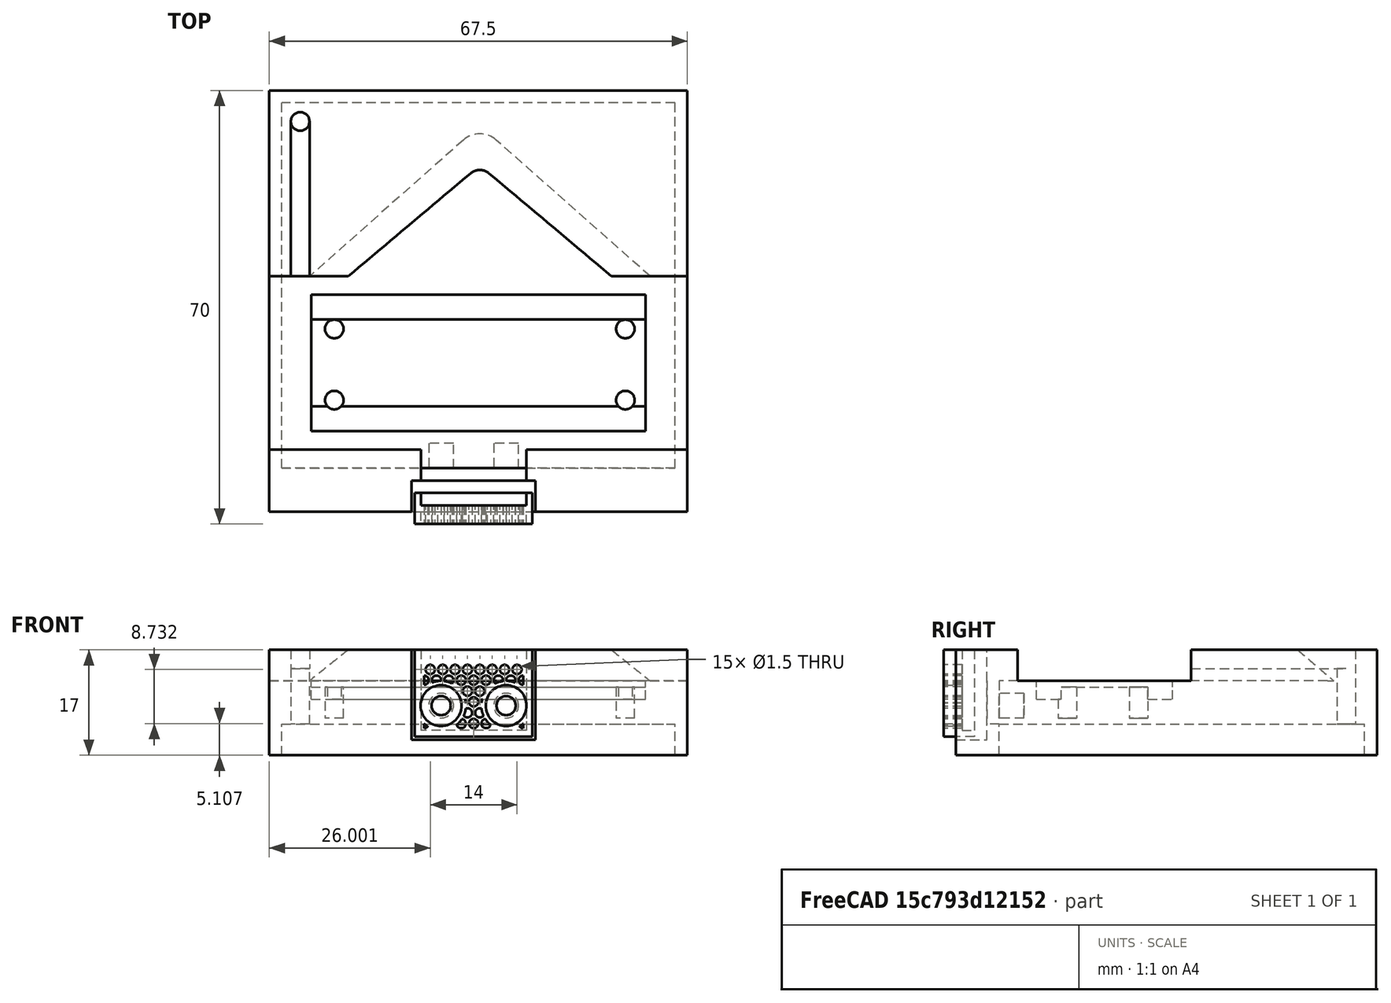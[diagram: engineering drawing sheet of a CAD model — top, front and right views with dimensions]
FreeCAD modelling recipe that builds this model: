
FCSTD DOCUMENT  (FreeCAD 0.20R29410 (Git))
Label: Weatherstation
License: All rights reserved
LicenseURL: https://en.wikipedia.org/wiki/All_rights_reserved
objects: Part::Cylinder×13, Part::Box×10, Sketcher::SketchObject×8, PartDesign::Body×6, PartDesign::Pad×5, Part::Cut×5, Part::MultiFuse×4, Part::FeaturePython×3, Mesh::Feature×2, Part::Extrusion×1, PartDesign::AdditiveLoft×1, Part::MultiCommon×1
note: 62 computed .brp shape members not serialized (recipe doc carries the construction recipe); baked Part::Feature solids carry a one-line shape summary decoded from their .brp

FEATURE [Sketcher::SketchObject] Sketch
  FullyConstrained = true
  MapMode = 5
  Support = -> [XY_Plane]
  sketch-geometry (4):
    g0: LineSegment StartX=19 StartY=19 StartZ=0 EndX=86.5 EndY=19 EndZ=0
    g1: LineSegment StartX=86.5 StartY=19 StartZ=0 EndX=86.5 EndY=82 EndZ=0
    g2: LineSegment StartX=86.5 StartY=82 StartZ=0 EndX=19 EndY=82 EndZ=0
    g3: LineSegment StartX=19 StartY=82 StartZ=0 EndX=19 EndY=19 EndZ=0
  constraints (12):
    c: Coincident(g0,g1)
    c: Coincident(g1,g2)
    c: Coincident(g2,g3)
    c: Coincident(g3,g0)
    c: Horizontal(g0)
    c: Horizontal(g2)
    c: Vertical(g1)
    c: Vertical(g3)
    c: DistanceX(g-1,g0) = 19
    c: DistanceY(g-1,g0) = 19
    c: DistanceY(g1,g1) = 63
    c: DistanceX(g0,g0) = 67.5
FEATURE [PartDesign::Pad] Pad
  Direction = (0,0,1)
  Length = 12
  Length2 = 10
  Profile = -> Sketch
  ReferenceAxis = -> Sketch [N_Axis]
  Type = 0
FEATURE [PartDesign::Body] Body  label="Base"
  Group = -> [Sketch,Pad]
  Origin = -> Origin
  Placement = pos=(0,0,-2) rot=(0,0,1;0rad)
  Tip = -> Pad
FEATURE [Sketcher::SketchObject] Sketch001
  FullyConstrained = true
  MapMode = 5
  Support = -> [XY_Plane001]
  sketch-geometry (4):
    g0: LineSegment StartX=22.75 StartY=49 StartZ=0 EndX=76.75 EndY=49 EndZ=0
    g1: LineSegment StartX=76.75 StartY=49 StartZ=0 EndX=76.75 EndY=27 EndZ=0
    g2: LineSegment StartX=76.75 StartY=27 StartZ=0 EndX=22.75 EndY=27 EndZ=0
    g3: LineSegment StartX=22.75 StartY=27 StartZ=0 EndX=22.75 EndY=49 EndZ=0
  constraints (12):
    c: Coincident(g0,g1)
    c: Coincident(g1,g2)
    c: Coincident(g2,g3)
    c: Coincident(g3,g0)
    c: Horizontal(g0)
    c: Horizontal(g2)
    c: Vertical(g1)
    c: Vertical(g3)
    c: DistanceX(g0,g0) = 54
    c: DistanceY(g1,g1) = 22
    c: DistanceX(g-1,g2) = 22.75
    c: DistanceY(g-1,g2) = 27
FEATURE [PartDesign::Pad] Pad001
  Direction = (0,0,1)
  Length = 2
  Length2 = 10
  Profile = -> Sketch001
  ReferenceAxis = -> Sketch001 [N_Axis]
  Type = 0
FEATURE [PartDesign::Body] Body001  label="Pico sink"
  Group = -> [Sketch001,Pad001]
  Origin = -> Origin001
  Placement = pos=(0,0,9) rot=(0,0,1;0rad)
  Tip = -> Pad001
FEATURE [Part::Cylinder] Cylinder  label="Pico Screw 1"
  Angle = 360
  AttacherType = Attacher::AttachEngine3D
  FirstAngle = 0
  Height = 10
  Placement = pos=(26.5,32,4) rot=(0,0,1;0rad)
  Radius = 1.5
  SecondAngle = 0
FEATURE [Part::Cylinder] Cylinder001  label="Pico Screw 2"
  Angle = 360
  AttacherType = Attacher::AttachEngine3D
  FirstAngle = 0
  Height = 10
  Placement = pos=(26.5,43.5,4) rot=(0,0,1;0rad)
  Radius = 1.5
  SecondAngle = 0
FEATURE [Part::Cylinder] Cylinder002  label="Pico Screw 3"
  Angle = 360
  AttacherType = Attacher::AttachEngine3D
  FirstAngle = 0
  Height = 10
  Placement = pos=(73.5,43.5,4) rot=(0,0,1;0rad)
  Radius = 1.5
  SecondAngle = 0
FEATURE [Part::Cylinder] Cylinder003  label="Pico Screw 4"
  Angle = 360
  AttacherType = Attacher::AttachEngine3D
  FirstAngle = 0
  Height = 10
  Placement = pos=(73.5,32,4) rot=(0,0,1;0rad)
  Radius = 1.5
  SecondAngle = 0
FEATURE [Part::Cylinder] Cylinder004  label="bme280 screw 1"
  Angle = 360
  AttacherType = Attacher::AttachEngine3D
  FirstAngle = 0
  Height = 10
  Placement = pos=(45.75,26,8) rot=(1,0,0;1.5708rad)
  Radius = 2
  SecondAngle = 0
FEATURE [Part::Cylinder] Cylinder005  label="bme280 screw 2"
  Angle = 360
  AttacherType = Attacher::AttachEngine3D
  FirstAngle = 0
  Height = 10
  Placement = pos=(56.25,26,8) rot=(1,0,0;1.5708rad)
  Radius = 2
  SecondAngle = 0
FEATURE [Sketcher::SketchObject] Sketch002
  FullyConstrained = true
  MapMode = 5
  Placement = pos=(0,0,0) rot=(1,0,0;1.5708rad)
  Support = -> [XZ_Plane002]
  sketch-geometry (4):
    g0: LineSegment StartX=41.5 StartY=13 StartZ=0 EndX=60.5 EndY=13 EndZ=0
    g1: LineSegment StartX=60.5 StartY=13 StartZ=0 EndX=60.5 EndY=-1 EndZ=0
    g2: LineSegment StartX=60.5 StartY=-1 StartZ=0 EndX=41.5 EndY=-1 EndZ=0
    g3: LineSegment StartX=41.5 StartY=-1 StartZ=0 EndX=41.5 EndY=13 EndZ=0
  constraints (12):
    c: Coincident(g0,g1)
    c: Coincident(g1,g2)
    c: Coincident(g2,g3)
    c: Coincident(g3,g0)
    c: Horizontal(g0)
    c: Horizontal(g2)
    c: Vertical(g1)
    c: Vertical(g3)
    c: DistanceX(g0,g0) = 19
    c: DistanceY(g1,g1) = 14
    c: DistanceX(g-1,g2) = 41.5
    c: DistanceY(g-1,g2) = -1
FEATURE [PartDesign::Pad] Pad002
  Direction = (0,-1,-2e-16)
  Length = 5
  Length2 = 10
  Placement = pos=(0,0,0) rot=(1,0,0;1.5708rad)
  Profile = -> Sketch002
  ReferenceAxis = -> Sketch002 [N_Axis]
  Type = 0
FEATURE [PartDesign::Body] Body002  label="bme280 protector"
  Group = -> [Sketch002,Pad002]
  Origin = -> Origin002
  Placement = pos=(0,17,0) rot=(0,0,1;0rad)
  Tip = -> Pad002
FEATURE [Part::Box] Box  label="bme280 hole"
  AttacherType = Attacher::AttachEngine3D
  Height = 12
  Length = 17
  Placement = pos=(42.5,20,-1) rot=(0,0,1;0rad)
  Width = 2
FEATURE [Part::Cylinder] Cylinder006  label="bme280 screw 3"
  Angle = 360
  AttacherType = Attacher::AttachEngine3D
  FirstAngle = 0
  Height = 10
  Placement = pos=(45.75,20,7) rot=(1,0,0;1.5708rad)
  Radius = 1.55
  SecondAngle = 0
FEATURE [Part::Cylinder] Cylinder007  label="bme280 screw 4"
  Angle = 360
  AttacherType = Attacher::AttachEngine3D
  FirstAngle = 0
  Height = 10
  Placement = pos=(56.25,20,7) rot=(1,0,0;1.5708rad)
  Radius = 1.55
  SecondAngle = 0
FEATURE [Part::Box] Box001  label="Pico Con 1"
  AttacherType = Attacher::AttachEngine3D
  Height = 2
  Length = 54
  Placement = pos=(22.75,45,7) rot=(0,0,1;0rad)
  Width = 4
FEATURE [Part::Box] Box002  label="Pico Con 2"
  AttacherType = Attacher::AttachEngine3D
  Height = 2
  Length = 54
  Placement = pos=(22.75,27,7) rot=(0,0,1;0rad)
  Width = 4
FEATURE [Part::Box] Box003  label="bme280 Iron 1"
  AttacherType = Attacher::AttachEngine3D
  Height = 5
  Length = 17
  Placement = pos=(42.5,17,-1) rot=(0,0,1;0rad)
  Width = 5
FEATURE [Part::FeaturePython] BooleanFragments001  label="bme280"  # WARN: FeaturePython — macro-defined, semantics opaque (R4)
  Mode = 0
  Objects = -> [Cylinder005,Cylinder004,Box003,Box]
  Placement = pos=(1,41,14) rot=(1,0,0;3.14159rad)
  Tolerance = 0
FEATURE [Part::Box] Box004  label="Power Pack"
  AttacherType = Attacher::AttachEngine3D
  Height = 15
  Length = 63.5
  Placement = pos=(21,21,-12) rot=(0,0,1;0rad)
  Width = 59
FEATURE [Part::Cylinder] Cylinder008  label="bme280 screw 005"
  Angle = 360
  AttacherType = Attacher::AttachEngine3D
  FirstAngle = 0
  Height = 2
  Placement = pos=(45.75,14,7) rot=(1,0,0;1.5708rad)
  Radius = 3.3
  SecondAngle = 0
FEATURE [Part::Cylinder] Cylinder009  label="bme280 screw 006"
  Angle = 360
  AttacherType = Attacher::AttachEngine3D
  FirstAngle = 0
  Height = 2
  Placement = pos=(56.25,14,7) rot=(1,0,0;1.5708rad)
  Radius = 3.3
  SecondAngle = 0
FEATURE [Part::Box] Box005  label="bme281"
  AttacherType = Attacher::AttachEngine3D
  Height = 14
  Length = 17
  Placement = pos=(42.5,15,-3) rot=(0,0,1;0rad)
  Width = 2
FEATURE [Sketcher::SketchObject] Sketch003
  FullyConstrained = false
  Placement = pos=(0,0,0) rot=(1,0,0;1.5708rad)
  sketch-geometry (5):
    g0: Circle CenterX=7.86917 CenterY=53.8929 CenterZ=0 NormalX=0 NormalY=0 NormalZ=1 AngleXU=0 Radius=0.75
    g1: LineSegment StartX=7.86917 StartY=53.8929 StartZ=0 EndX=9.86917 EndY=53.8929 EndZ=0
    g2: LineSegment StartX=9.86917 StartY=53.8929 StartZ=0 EndX=8.86917 EndY=52.1609 EndZ=0
    g3: LineSegment StartX=8.86917 StartY=52.1609 StartZ=0 EndX=7.86917 EndY=53.8929 EndZ=0
    g4: Circle CenterX=8.86917 CenterY=52.1609 CenterZ=0 NormalX=0 NormalY=0 NormalZ=1 AngleXU=0 Radius=0.75
  constraints (11):
    c: Radius(g0) = 0.75
    c: Coincident(g1,g0)
    c: Horizontal(g1)
    c: Coincident(g1,g2)
    c: Coincident(g2,g3)
    c: Coincident(g3,g1)
    c: DistanceX(g1,g1) = 2
    c: Equal(g1,g2)
    c: Equal(g2,g3)
    c: Coincident(g4,g2)
    c: Equal(g0,g4)
FEATURE [Part::FeaturePython] Array  # Draft array (typed FeaturePython)
  AlwaysSyncPlacement = false
  Angle = 360
  ArrayType = 0
  Axis = (0,0,1)
  Base = -> Sketch003
  Center = (0,0,0)
  Count = 30
  ExpandArray = false
  Fuse = false
  IntervalAxis = (0,0,0)
  IntervalX = (2,0,0)
  IntervalY = (0,2,0)
  IntervalZ = (0,0,3.5)
  NumberCircles = 3
  NumberPolar = 5
  NumberX = 10
  NumberY = 1
  NumberZ = 3
  Placement = pos=(33.13,0,-51) rot=(0,0,1;0rad)
  PlacementList = 30 placements: [(0,0,0),(0,0,3.5),(0,0,7),(2,0,0),(2,0,3.5),(2,0,7),(4,0,0),(4,0,3.5),(4,0,7),(6,0,0),(6,0,3.5),(6,0,7),(8,0,0),(8,0,3.5),(8,0,7),(10,0,0),(10,0,3.5),(10,0,7),(12,0,0),(12,0,3.5),(12,0,7),(14,0,0),(14,0,3.5),(14,0,7),(16,0,0),(16,0,3.5),(16,0,7),(18,0,0),(18,0,3.5),(18,0,7)]
  RadialDistance = 50
  ScaleList = (30) [(1,1,1),(1,1,1),(1,1,1),(1,1,1),(1,1,1),(1,1,1),(1,1,1),(1,1,1),(1,1,1),(1,1,1),(1,1,1),(1,1,1),(1,1,1),(1,1,1),(1,1,1),(1,1,1),(1,1,1),(1,1,1),+12 more]
  Symmetry = 1
  TangentialDistance = 25
FEATURE [Part::Extrusion] Extrude
  Base = -> Array
  Dir = (0,1,0)
  DirMode = 2
  FaceMakerClass = Part::FaceMakerBullseye
  LengthFwd = 10
  LengthRev = 0
  Placement = pos=(0,8,0) rot=(0,0,1;0rad)
  Solid = true
  Symmetric = false
FEATURE [Part::Box] Box006  label="bme282"
  AttacherType = Attacher::AttachEngine3D
  Height = 12
  Length = 16
  Placement = pos=(43,9,-1) rot=(0,0,1;0rad)
  Width = 12
FEATURE [Part::Cylinder] Cylinder010  label="bme280 screw 007"
  Angle = 360
  AttacherType = Attacher::AttachEngine3D
  FirstAngle = 0
  Height = 18
  Placement = pos=(45.75,26,7) rot=(1,0,0;1.5708rad)
  Radius = 4
  SecondAngle = 0
FEATURE [Part::Cylinder] Cylinder011  label="bme280 screw 008"
  Angle = 360
  AttacherType = Attacher::AttachEngine3D
  FirstAngle = 0
  Height = 20
  Placement = pos=(56.25,26,7) rot=(1,0,0;1.5708rad)
  Radius = 4
  SecondAngle = 0
FEATURE [Sketcher::SketchObject] Sketch004
  FullyConstrained = true
  MapMode = 5
  Support = -> [XY_Plane003]
  sketch-geometry (4):
    g0: LineSegment StartX=19 StartY=52 StartZ=0 EndX=86.5 EndY=52 EndZ=0
    g1: LineSegment StartX=86.5 StartY=52 StartZ=0 EndX=86.5 EndY=82 EndZ=0
    g2: LineSegment StartX=86.5 StartY=82 StartZ=0 EndX=19 EndY=82 EndZ=0
    g3: LineSegment StartX=19 StartY=82 StartZ=0 EndX=19 EndY=52 EndZ=0
  constraints (12):
    c: Coincident(g0,g1)
    c: Coincident(g1,g2)
    c: Coincident(g2,g3)
    c: Coincident(g3,g0)
    c: Horizontal(g0)
    c: Horizontal(g2)
    c: Vertical(g1)
    c: Vertical(g3)
    c: DistanceX(g-1,g0) = 19
    c: DistanceY(g1,g1) = 30
    c: DistanceX(g0,g0) = 67.5
    c: DistanceY(g-1,g2) = 82
FEATURE [PartDesign::Pad] Pad003
  Direction = (0,0,1)
  Length = 5
  Length2 = 10
  Profile = -> Sketch004
  ReferenceAxis = -> Sketch004 [N_Axis]
  Type = 0
FEATURE [PartDesign::Body] Body003  label="top base"
  Group = -> [Sketch004,Pad003]
  Origin = -> Origin003
  Placement = pos=(0,0,10) rot=(0,0,1;0rad)
  Tip = -> Pad003
FEATURE [Sketcher::SketchObject] Sketch005
  FullyConstrained = true
  MapMode = 5
  Support = -> [XY_Plane004]
  sketch-geometry (4):
    g0: LineSegment StartX=19 StartY=19 StartZ=0 EndX=86.5 EndY=19 EndZ=0
    g1: LineSegment StartX=86.5 StartY=19 StartZ=0 EndX=86.5 EndY=24 EndZ=0
    g2: LineSegment StartX=86.5 StartY=24 StartZ=0 EndX=19 EndY=24 EndZ=0
    g3: LineSegment StartX=19 StartY=24 StartZ=0 EndX=19 EndY=19 EndZ=0
  constraints (12):
    c: Coincident(g0,g1)
    c: Coincident(g1,g2)
    c: Coincident(g2,g3)
    c: Coincident(g3,g0)
    c: Horizontal(g0)
    c: Horizontal(g2)
    c: Vertical(g1)
    c: Vertical(g3)
    c: DistanceX(g-1,g0) = 19
    c: DistanceY(g1,g1) = 5
    c: DistanceX(g0,g0) = 67.5
    c: DistanceY(g-1,g0) = 19
FEATURE [PartDesign::Pad] Pad004
  Direction = (0,0,1)
  Length = 5
  Length2 = 10
  Profile = -> Sketch005
  ReferenceAxis = -> Sketch005 [N_Axis]
  Type = 0
FEATURE [PartDesign::Body] Body004  label="bottom base"
  Group = -> [Sketch005,Pad004]
  Origin = -> Origin004
  Placement = pos=(0,0,10) rot=(0,0,1;0rad)
  Tip = -> Pad004
FEATURE [Sketcher::SketchObject] Sketch008
  FullyConstrained = true
  MapMode = 5
  Placement = pos=(0,0,6) rot=(0,0,1;0rad)
  sketch-geometry (4):
    g0: LineSegment StartX=33 StartY=51 StartZ=0 EndX=51.7227 EndY=66.539 EndZ=0
    g1: LineSegment StartX=54.2773 StartY=66.539 StartZ=0 EndX=73 EndY=51 EndZ=0
    g2: LineSegment StartX=73 StartY=51 StartZ=0 EndX=33 EndY=51 EndZ=0
    g3: ArcOfCircle CenterX=53 CenterY=65 CenterZ=0 NormalX=0 NormalY=0 NormalZ=1 AngleXU=0 Radius=2 StartAngle=0.878055 EndAngle=2.26354
  constraints (11):
    c: Coincident(g1,g2)
    c: Coincident(g2,g0)
    c: Horizontal(g2)
    c: Equal(g0,g1)
    c: DistanceX(g0,g1) = 40
    c: DistanceY(g-1,g0) = 51
    c: Tangent(g0,g3) = 1.5708
    c: Tangent(g1,g3) = 1.5708
    c: Radius(g3) = 2
    c: DistanceX(g-1,g3) = 53
    c: DistanceY(g-1,g3) = 65
FEATURE [Sketcher::SketchObject] Sketch009
  FullyConstrained = true
  MapMode = 5
  sketch-geometry (4):
    g0: LineSegment StartX=50.3488 StartY=72.9952 StartZ=0 EndX=25.5 EndY=51 EndZ=0
    g1: LineSegment StartX=25.5 StartY=51 StartZ=0 EndX=80.5 EndY=51 EndZ=0
    g2: LineSegment StartX=80.5 StartY=51 StartZ=0 EndX=55.6512 EndY=72.9952 EndZ=0
    g3: ArcOfCircle CenterX=53 CenterY=70 CenterZ=0 NormalX=0 NormalY=0 NormalZ=1 AngleXU=0 Radius=4 StartAngle=0.84624 EndAngle=2.29535
  constraints (11):
    c: Coincident(g0,g1)
    c: Horizontal(g1)
    c: Coincident(g1,g2)
    c: Equal(g2,g0)
    c: Tangent(g0,g3) = -1.5708
    c: Tangent(g2,g3) = -1.5708
    c: Radius(g3) = 4
    c: DistanceX(g1,g1) = 55
    c: DistanceX(g-1,g3) = 53
    c: DistanceY(g-1,g0) = 51
    c: DistanceY(g-1,g3) = 70
FEATURE [PartDesign::AdditiveLoft] AdditiveLoft
  Closed = false
  Placement = pos=(0,0,6) rot=(0,0,1;0rad)
  Profile = -> Sketch008
  Ruled = false
  Sections = -> [Sketch009]
FEATURE [PartDesign::Body] Body006  label="Anker"
  Group = -> [Sketch009,Sketch008,AdditiveLoft]
  Origin = -> Origin006
  Placement = pos=(0,1,10) rot=(0,0,1;0rad)
  Tip = -> AdditiveLoft
FEATURE [Part::MultiCommon] Common  label="Grid"
  Shapes = -> [Box006,Extrude]
FEATURE [Part::MultiFuse] Fusion  label="Screwholes"
  Shapes = -> [Cylinder010,Cylinder011]
FEATURE [Part::Cut] Cut  label="Grid cutout"
  Base = -> Common
  Tool = -> Fusion
FEATURE [Part::MultiFuse] Fusion003  label="bme280 cutout"
  Placement = pos=(0,0,1) rot=(0,0,1;0rad)
  Shapes = -> [Box005,Cylinder009,Cylinder008,Cylinder007,Cylinder006,Cut]
FEATURE [Part::Cut] Cut005  label="bme280 protector001"
  Base = -> Body002
  Placement = pos=(103,0,14) rot=(0,1,0;3.14159rad)
  Tool = -> Fusion003
FEATURE [Part::Box] Box007  label="Würfel"
  AttacherType = Attacher::AttachEngine3D
  Height = 17
  Length = 67.5
  Placement = pos=(19,14,-2) rot=(0,0,1;0rad)
  Width = 5
FEATURE [Part::Box] Box008  label="Würfel001"
  AttacherType = Attacher::AttachEngine3D
  Height = 15
  Length = 20
  Placement = pos=(42,9,0.5) rot=(0,0,1;0rad)
  Width = 10
FEATURE [Part::Cut] Cut006
  Base = -> Box007
  Tool = -> Box008
FEATURE [Part::MultiFuse] Fusion001  label="Base Complete"
  Shapes = -> [Body004,Body003,Body,Cut006]
FEATURE [Part::Cylinder] Cylinder012  label="Zylinder"
  Angle = 360
  AttacherType = Attacher::AttachEngine3D
  FirstAngle = 0
  Height = 40
  Placement = pos=(21,77,-2) rot=(0,0,1;0rad)
  Radius = 1.5
  SecondAngle = 0
FEATURE [Part::Box] Box009  label="Würfel002"
  AttacherType = Attacher::AttachEngine3D
  Height = 3
  Length = 3
  Placement = pos=(19.5,50,12) rot=(0,0,1;0rad)
  Width = 27
FEATURE [Part::FeaturePython] BooleanFragments  label="Pico Holes"  # WARN: FeaturePython — macro-defined, semantics opaque (R4)
  Mode = 0
  Objects = -> [Body001,Cylinder,Cylinder001,Cylinder002,Cylinder003,Box001,Box002,Cylinder012,Box009]
  Placement = pos=(3,0,0) rot=(0,0,1;0rad)
  Tolerance = 0
FEATURE [Part::MultiFuse] Fusion002  label="Cuts"
  Shapes = -> [Body006,BooleanFragments001,BooleanFragments]
FEATURE [Part::Cut] Cut003
  Base = -> Fusion001
  Tool = -> Fusion002
FEATURE [Part::Cut] Cut004  label="Base002"
  Base = -> Cut003
  Tool = -> Box004
FEATURE [Mesh::Feature] Mesh  label="bme280 protector001 (Meshed)"
FEATURE [Mesh::Feature] Mesh001  label="Base002 (Meshed)"
